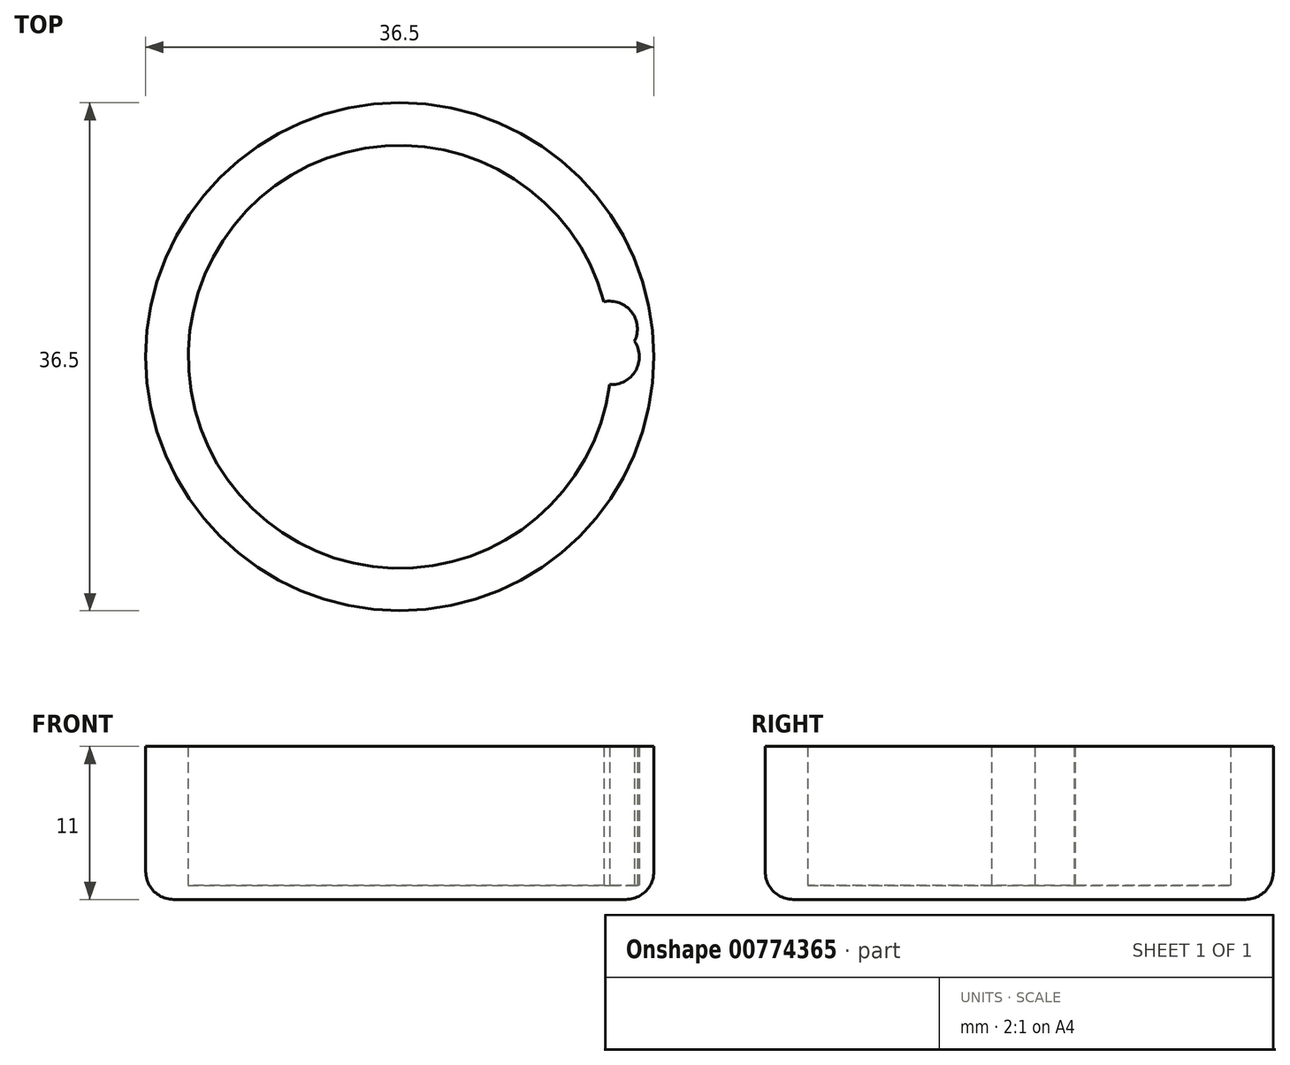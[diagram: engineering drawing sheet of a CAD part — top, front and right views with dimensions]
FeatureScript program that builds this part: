
annotation { "Feature Type Name" : "Feature", "Feature Type Description" : "" }
export const myFeature = defineFeature(function(context is Context, id is Id, definition is map)
    precondition{}
    {
        {
            var Q0;
            Q0=qCreatedBy(makeId("Top.planeOp"),FACE);
            var sketch = newSketch(context, id + "F0", { "sketchPlane" : qUnion([Q0])});
            skArc(sketch, "E0", {"start": v(14.68, 3.96) * mm, "mid": v(-15.17, -1) * mm, "end": v(15.07, -2) * mm});
            skCircle(sketch, "E1", {"center": v(0, 0) * mm, "radius": 18.25 * mm});
            skArc(sketch, "E2", {"start": v(15.07, -2) * mm, "mid": v(16.93, -1) * mm, "end": v(16.86, 1.11) * mm});
            skArc(sketch, "E3", {"start": v(16.86, 1.11) * mm, "mid": v(16.65, 3.21) * mm, "end": v(14.68, 3.96) * mm});
            skSolve(sketch);
        }
        {
            var Q0;
            {var subQ0=sQuery(id+"F0.wireOp",EDGE,"E2");var subQ1=sQuery(id+"F0.wireOp",EDGE,"E0");var subQ2=makeQuery(id+"F0.imprint","INTERSECT",VERTEX,{"disambiguationData":[OD(0.0)],"derivedFrom":[subQ1,subQ0]});Q0=makeQuery(id+"F0.imprint","IMPRINT",FACE,{"disambiguationData":[TD([[makeQuery(id+"F0.imprint","IMPRINT",EDGE,{"disambiguationData":[TD([[subQ2,1.0]])],"derivedFrom":subQ1}),1.0]])]});}
            var Q1;
            {var subQ0=sQuery(id+"F0.wireOp",EDGE,"E2");var subQ1=sQuery(id+"F0.wireOp",EDGE,"E0");var subQ2=makeQuery(id+"F0.imprint","INTERSECT",VERTEX,{"disambiguationData":[OD(0.0)],"derivedFrom":[subQ1,subQ0]});Q1=makeQuery(id+"F0.imprint","IMPRINT",FACE,{"disambiguationData":[TD([[makeQuery(id+"F0.imprint","IMPRINT",EDGE,{"disambiguationData":[TD([[subQ2,-1.0]])],"derivedFrom":subQ1}),1.0]])]});}
            var Q2;
            Q2=makeQuery(id+"F0.imprint","IMPRINT",FACE,{"disambiguationData":[TD([[makeQuery(id+"F0.imprint","IMPRINT",EDGE,{"derivedFrom":sQuery(id+"F0.wireOp",EDGE,"E1")}),1.0]])]});
            var Q3;
            {var subQ0=sQuery(id+"F0.wireOp",EDGE,"E2");var subQ1=sQuery(id+"F0.wireOp",EDGE,"E0");var subQ2=makeQuery(id+"F0.imprint","INTERSECT",VERTEX,{"disambiguationData":[OD(0.0)],"derivedFrom":[subQ1,subQ0]});Q3=makeQuery(id+"F0.imprint","IMPRINT",FACE,{"disambiguationData":[TD([[makeQuery(id+"F0.imprint","IMPRINT",EDGE,{"disambiguationData":[TD([[subQ2,-1.0]])],"derivedFrom":subQ1}),-1.0]])]});}
            extrude(context, id + "F1", {"entities" : qUnion([Q0, Q1, Q2, Q3]), "oppositeDirection" : true, "depth" : 1 * mm, "offsetDistance" : 25 * mm});
        }
        {
            var Q0;
            Q0=makeQuery(id+"F0.imprint","IMPRINT",FACE,{"disambiguationData":[TD([[makeQuery(id+"F0.imprint","IMPRINT",EDGE,{"derivedFrom":sQuery(id+"F0.wireOp",EDGE,"E1")}),1.0]])]});
            extrude(context, id + "F2", {"entities" : qUnion([Q0]), "operationType" : NewBodyOperationType.ADD, "depth" : 10 * mm, "offsetDistance" : 25 * mm});
        }
        {
            var Q0;
            Q0=makeQuery(id+"F1.opExtrude","CAP_EDGE",EDGE,{"disambiguationData":[OSD([sQuery(id+"F0.wireOp",EDGE,"E1")])],"isStart":false});
            fillet(context, id + "F3", {"entities" : qUnion([Q0]), "radius" : 2 * mm, "tangentPropagation" : true, "allowEdgeOverflow" : false});
        }
    });
